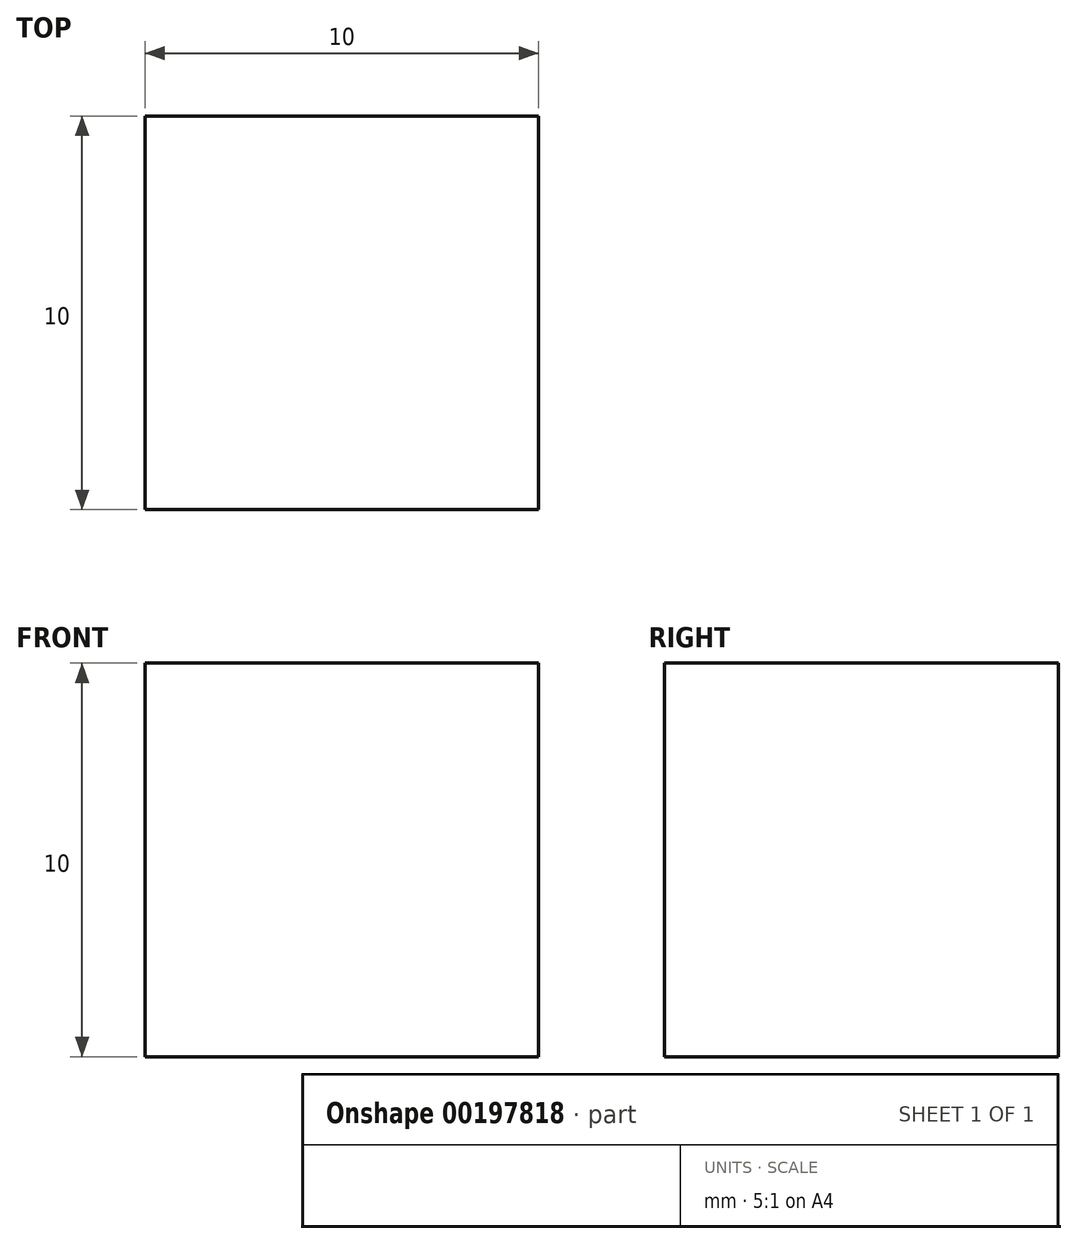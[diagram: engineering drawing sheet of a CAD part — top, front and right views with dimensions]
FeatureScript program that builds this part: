
annotation { "Feature Type Name" : "Feature", "Feature Type Description" : "" }
export const myFeature = defineFeature(function(context is Context, id is Id, definition is map)
    precondition{}
    {
        {
            var Q0;
            Q0=qCreatedBy(makeId("Front.planeOp"),FACE);
            var sketch = newSketch(context, id + "F0", { "sketchPlane" : qUnion([Q0])});
            skLineSegment(sketch, "E0.bottom", {"start": v(5, 5) * mm, "end": v(-5, 5) * mm});
            skLineSegment(sketch, "E0.top", {"start": v(5, -5) * mm, "end": v(-5, -5) * mm});
            skLineSegment(sketch, "E0.left", {"start": v(5, 5) * mm, "end": v(5, -5) * mm});
            skLineSegment(sketch, "E0.right", {"start": v(-5, 5) * mm, "end": v(-5, -5) * mm});
            skPoint(sketch, "E0.middle", {"position": v(0, 0) * mm});
            skSolve(sketch);
        }
        {
            var Q0;
            Q0=makeQuery(id+"F0.imprint","IMPRINT",FACE,{"disambiguationData":[TD([[makeQuery(id+"F0.imprint","IMPRINT",EDGE,{"derivedFrom":sQuery(id+"F0.wireOp",EDGE,"E0.bottom")}),1.0]])]});
            extrude(context, id + "F1", {"entities" : qUnion([Q0]), "depth" : 10 * mm});
        }
    });
